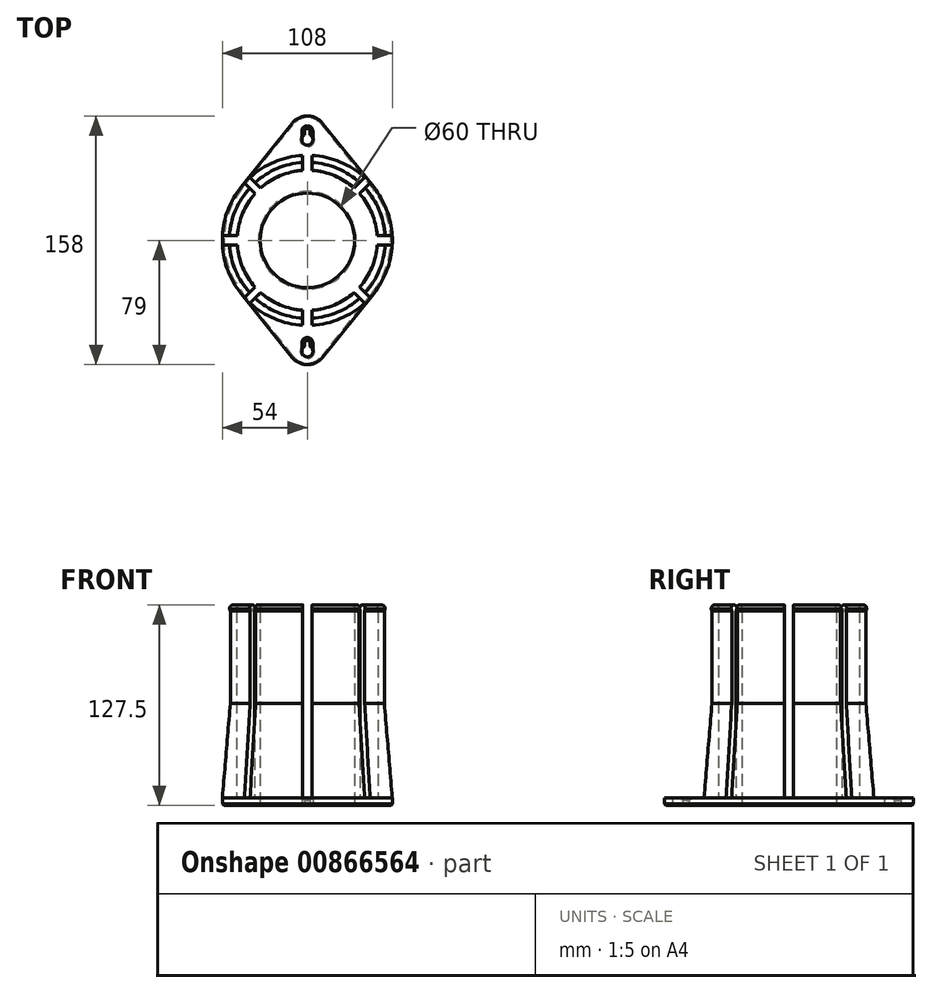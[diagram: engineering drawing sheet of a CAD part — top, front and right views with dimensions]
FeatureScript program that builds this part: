
annotation { "Feature Type Name" : "Feature", "Feature Type Description" : "" }
export const myFeature = defineFeature(function(context is Context, id is Id, definition is map)
    precondition{}
    {
        {
            assignVariable(context, id + "F0", {"name" : "plate", "anyValue" : 5});
        }
        {
            var Q0;
            Q0=qCreatedBy(makeId("Front.planeOp"),FACE);
            var sketch = newSketch(context, id + "F1", { "sketchPlane" : qUnion([Q0])});
            skLineSegment(sketch, "E0.bottom", {"start": v(0, 0) * mm, "end": v(-54, 0) * mm});
            skLineSegment(sketch, "E0.top", {"start": v(0, 5) * mm, "end": v(-54, 5) * mm});
            skLineSegment(sketch, "E0.left", {"start": v(0, 0) * mm, "end": v(0, 5) * mm});
            skLineSegment(sketch, "E0.right", {"start": v(-54, 0) * mm, "end": v(-54, 5) * mm});
            skLineSegment(sketch, "E1", {"start": v(-45, 125) * mm, "end": v(-49, 125) * mm});
            skArc(sketch, "E2", {"start": v(-49, 123.5) * mm, "mid": v(-47, 122.5) * mm, "end": v(-45, 123.5) * mm});
            skLineSegment(sketch, "E3", {"start": v(-47, 125) * mm, "end": v(-41.45, 125) * mm, "construction": true});
            skLineSegment(sketch, "E4", {"start": v(-47, 125) * mm, "end": v(-55.3, 125) * mm, "construction": true});
            skLineSegment(sketch, "E5", {"start": v(-49.5, 125) * mm, "end": v(-49, 123.5) * mm});
            skLineSegment(sketch, "E6", {"start": v(-45, 123.5) * mm, "end": v(-44.5, 125) * mm});
            skArc(sketch, "E7.trimOffspring", {"start": v(-44.5, 125) * mm, "mid": v(-47, 127.5) * mm, "end": v(-49.5, 125) * mm});
            skLineSegment(sketch, "E8", {"start": v(-45, 123.5) * mm, "end": v(-45, 5) * mm});
            skLineSegment(sketch, "E9", {"start": v(-49, 123.5) * mm, "end": v(-49, 5) * mm});
            skLineSegment(sketch, "E10", {"start": v(-54, 5) * mm, "end": v(-49, 65) * mm});
            skLineSegment(sketch, "E11", {"start": v(0, 0) * mm, "end": v(0, 112.8) * mm, "construction": true});
            skSolve(sketch);
        }
        {
            var Q0;
            Q0 = qSketchRegion(id + "F1", true);
            var Q1;
            Q1=sQuery(id+"F1.wireOp",EDGE,"E11");
            revolve(context, id + "F2", {"surfaceOperationType" : NewSurfaceOperationType.NEW, "entities" : qUnion([Q0]), "axis" : qUnion([Q1]), "revolveType" : RevolveType.FULL});
        }
        {
            var Q0;
            Q0=qCreatedBy(makeId("Top.planeOp"),FACE);
            var sketch = newSketch(context, id + "F3", { "sketchPlane" : qUnion([Q0])});
            skArc(sketch, "E12", {"start": v(9.77, 74.3) * mm, "mid": v(0, 79) * mm, "end": v(-9.77, 74.3) * mm});
            skArc(sketch, "E13", {"start": v(-42.2, 33.7) * mm, "mid": v(-54, 0) * mm, "end": v(-42.2, -33.7) * mm});
            skLineSegment(sketch, "E14", {"start": v(-72.22, 0) * mm, "end": v(71.62, 0) * mm, "construction": true});
            skLineSegment(sketch, "E15", {"start": v(-9.77, 74.3) * mm, "end": v(-42.2, 33.7) * mm});
            skLineSegment(sketch, "E16", {"start": v(9.77, 74.3) * mm, "end": v(42.2, 33.7) * mm});
            skLineSegment(sketch, "E17.MirrorCS", {"start": v(-9.77, -74.3) * mm, "end": v(-42.2, -33.7) * mm});
            skArc(sketch, "E18.MirrorCS", {"start": v(9.77, -74.3) * mm, "mid": v(0, -79) * mm, "end": v(-9.77, -74.3) * mm});
            skLineSegment(sketch, "E19.MirrorCS", {"start": v(9.77, -74.3) * mm, "end": v(42.2, -33.7) * mm});
            skArc(sketch, "E20.trimOffspring", {"start": v(42.2, -33.7) * mm, "mid": v(54, 0) * mm, "end": v(42.2, 33.7) * mm});
            skCircle(sketch, "E21", {"center": v(0, 0) * mm, "radius": 30 * mm});
            skCircle(sketch, "E22", {"center": v(0, 69.25) * mm, "radius": 1.75 * mm});
            skCircle(sketch, "E23", {"center": v(0, 64) * mm, "radius": 3.5 * mm});
            skCircle(sketch, "E24", {"center": v(0, -70.5) * mm, "radius": 3.5 * mm});
            skCircle(sketch, "E25", {"center": v(0, -65.25) * mm, "radius": 1.75 * mm});
            skLineSegment(sketch, "E26", {"start": v(-1.75, -65.25) * mm, "end": v(-1.75, -67.47) * mm});
            skLineSegment(sketch, "E27", {"start": v(1.75, -65.25) * mm, "end": v(1.75, -67.47) * mm});
            skLineSegment(sketch, "E28", {"start": v(-1.75, 69.25) * mm, "end": v(-1.75, 67.03) * mm});
            skLineSegment(sketch, "E29", {"start": v(1.75, 69.25) * mm, "end": v(1.75, 67.03) * mm});
            skSolve(sketch);
        }
        {
            var Q0;
            Q0 = qSketchRegion(id + "F3", true);
            var Q1;
            {var subQ0=sQuery(id+"F3.wireOp",EDGE,"f2jhoplT-4Byn-C6TP-uQtg-5tTXQIExNbQD");var subQ1=sQuery(id+"F3.wireOp",EDGE,"0pogwlZP-BW9K-9Tnw-1bp1-9pxBOHaQZQxX");var subQ2=makeQuery(id+"F3.imprint","INTERSECT",VERTEX,{"disambiguationData":[OD(0.0)],"derivedFrom":[subQ1,subQ0]});Q1=makeQuery(id+"F3.imprint","IMPRINT",FACE,{"disambiguationData":[TD([[makeQuery(id+"F3.imprint","IMPRINT",EDGE,{"disambiguationData":[TD([[subQ2,-1.0]])],"derivedFrom":subQ1}),-1.0]])]});}
            var Q2;
            {var subQ0=sQuery(id+"F3.wireOp",EDGE,"f2jhoplT-4Byn-C6TP-uQtg-5tTXQIExNbQD");var subQ1=sQuery(id+"F3.wireOp",EDGE,"0pogwlZP-BW9K-9Tnw-1bp1-9pxBOHaQZQxX");var subQ2=makeQuery(id+"F3.imprint","INTERSECT",VERTEX,{"disambiguationData":[OD(0.0)],"derivedFrom":[subQ1,subQ0]});Q2=makeQuery(id+"F3.imprint","IMPRINT",FACE,{"disambiguationData":[TD([[makeQuery(id+"F3.imprint","IMPRINT",EDGE,{"disambiguationData":[TD([[subQ2,1.0]])],"derivedFrom":subQ1}),1.0]])]});}
            extrude(context, id + "F4", {"entities" : qUnion([Q0, Q1, Q2]), "operationType" : NewBodyOperationType.ADD, "depth" : (getVariable(context, 'plate')) * mm, "offsetDistance" : 25 * mm});
        }
        {
            var Q0;
            {var subQ0=sQuery(id+"F3.wireOp",EDGE,"f2jhoplT-4Byn-C6TP-uQtg-5tTXQIExNbQD");var subQ1=sQuery(id+"F3.wireOp",EDGE,"0pogwlZP-BW9K-9Tnw-1bp1-9pxBOHaQZQxX");var subQ2=makeQuery(id+"F3.imprint","INTERSECT",VERTEX,{"disambiguationData":[OD(0.0)],"derivedFrom":[subQ1,subQ0]});Q0=makeQuery(id+"F3.imprint","IMPRINT",FACE,{"disambiguationData":[TD([[makeQuery(id+"F3.imprint","IMPRINT",EDGE,{"disambiguationData":[TD([[subQ2,1.0]])],"derivedFrom":subQ1}),1.0]])]});}
            var Q1;
            {var subQ0=sQuery(id+"F3.wireOp",EDGE,"f2jhoplT-4Byn-C6TP-uQtg-5tTXQIExNbQD");var subQ1=sQuery(id+"F3.wireOp",EDGE,"0pogwlZP-BW9K-9Tnw-1bp1-9pxBOHaQZQxX");var subQ2=makeQuery(id+"F3.imprint","INTERSECT",VERTEX,{"disambiguationData":[OD(0.0)],"derivedFrom":[subQ1,subQ0]});Q1=makeQuery(id+"F3.imprint","IMPRINT",FACE,{"disambiguationData":[TD([[makeQuery(id+"F3.imprint","IMPRINT",EDGE,{"disambiguationData":[TD([[subQ2,-1.0]])],"derivedFrom":subQ1}),-1.0]])]});}
            var Q2;
            Q2=makeQuery(id+"F3.imprint","IMPRINT",FACE,{"disambiguationData":[TD([[makeQuery(id+"F3.imprint","IMPRINT",EDGE,{"derivedFrom":sQuery(id+"F3.wireOp",EDGE,"E21")}),1.0]])]});
            extrude(context, id + "F5", {"entities" : qUnion([Q0, Q1, Q2]), "operationType" : NewBodyOperationType.REMOVE, "depth" : (getVariable(context, 'plate')) * mm, "offsetDistance" : 25 * mm});
        }
        {
            var Q0;
            Q0=qCreatedBy(makeId("Top.planeOp"),FACE);
            var sketch = newSketch(context, id + "F6", { "sketchPlane" : qUnion([Q0])});
            skLineSegment(sketch, "E30.bottom", {"start": v(3, 75) * mm, "end": v(-3, 75) * mm});
            skLineSegment(sketch, "E30.top", {"start": v(3, -75) * mm, "end": v(-3, -75) * mm});
            skLineSegment(sketch, "E30.left", {"start": v(3, 75) * mm, "end": v(3, -75) * mm});
            skLineSegment(sketch, "E30.right", {"start": v(-3, 75) * mm, "end": v(-3, -75) * mm});
            skPoint(sketch, "E30.middle", {"position": v(0, 0) * mm});
            skLineSegment(sketch, "E31", {"start": v(0, 0) * mm, "end": v(63.35, 63.35) * mm, "construction": true});
            skLineSegment(sketch, "E32", {"start": v(0, 0) * mm, "end": v(-59.23, 59.23) * mm, "construction": true});
            skLineSegment(sketch, "E33.MirrorCS", {"start": v(-75, 3) * mm, "end": v(75, 3) * mm});
            skLineSegment(sketch, "E34.MirrorCS", {"start": v(-75, -3) * mm, "end": v(75, -3) * mm});
            skLineSegment(sketch, "E35.MirrorCS", {"start": v(-75, -3) * mm, "end": v(-75, 3) * mm});
            skLineSegment(sketch, "E36.MirrorCS", {"start": v(75, -3) * mm, "end": v(75, 3) * mm});
            skLineSegment(sketch, "E37", {"start": v(-65.2, 68.73) * mm, "end": v(63.85, -60.32) * mm});
            skLineSegment(sketch, "E38", {"start": v(63.85, -60.32) * mm, "end": v(60.32, -63.85) * mm});
            skLineSegment(sketch, "E39", {"start": v(60.32, -63.85) * mm, "end": v(-68.73, 65.2) * mm});
            skLineSegment(sketch, "E40", {"start": v(-68.73, 65.2) * mm, "end": v(-65.2, 68.73) * mm});
            skLineSegment(sketch, "E41", {"start": v(0, 82.14) * mm, "end": v(0, -84.1) * mm, "construction": true});
            skLineSegment(sketch, "E42.MirrorCS", {"start": v(65.2, 68.73) * mm, "end": v(-63.85, -60.32) * mm});
            skLineSegment(sketch, "E43.MirrorCS", {"start": v(-60.32, -63.85) * mm, "end": v(68.73, 65.2) * mm});
            skLineSegment(sketch, "E44.MirrorCS", {"start": v(68.73, 65.2) * mm, "end": v(65.2, 68.73) * mm});
            skLineSegment(sketch, "E45.MirrorCS", {"start": v(-63.85, -60.32) * mm, "end": v(-60.32, -63.85) * mm});
            skSolve(sketch);
        }
        {
            var Q0;
            Q0 = qSketchRegion(id + "F6", true);
            extrude(context, id + "F7", {"entities" : qUnion([Q0]), "operationType" : NewBodyOperationType.REMOVE, "depth" : 150 * mm, "offsetDistance" : 25 * mm, "hasSecondDirection" : true, "secondDirectionOppositeDirection" : false, "secondDirectionDepth" : (getVariable(context, 'plate')) * mm});
        }
        {
            var Q0;
            Q0=makeQuery(id+"F4.opExtrude","CAP_EDGE",EDGE,{"disambiguationData":[OSD([sQuery(id+"F3.wireOp",EDGE,"E22")])],"isStart":false});
            var Q1;
            Q1=makeQuery(id+"F4.opExtrude","CAP_EDGE",EDGE,{"disambiguationData":[OSD([sQuery(id+"F3.wireOp",EDGE,"E25")])],"isStart":false});
            chamfer(context, id + "F8", {"entities" : qUnion([Q0, Q1]), "width" : 1.75 * mm, "tangentPropagation" : true});
        }
        {
            var Q0;
            Q0=makeQuery(id+"F4.boolean.opBoolean","MERGE",FACE,{"derivedFrom":[makeQuery(id+"F2.opRevolve","SWEPT_FACE",FACE,{"disambiguationData":[OSD([sQuery(id+"F1.wireOp",EDGE,"E0.bottom")])]}),makeQuery(id+"F4.opExtrude","CAP_FACE",FACE,{"disambiguationData":[OSD([sQuery(id+"F3.wireOp",EDGE,"E12"),sQuery(id+"F3.wireOp",EDGE,"E13"),sQuery(id+"F3.wireOp",EDGE,"E15"),sQuery(id+"F3.wireOp",EDGE,"E16"),sQuery(id+"F3.wireOp",EDGE,"E17.MirrorCS"),sQuery(id+"F3.wireOp",EDGE,"E18.MirrorCS"),sQuery(id+"F3.wireOp",EDGE,"E19.MirrorCS"),sQuery(id+"F3.wireOp",EDGE,"E20.trimOffspring"),sQuery(id+"F3.wireOp",EDGE,"E21"),sQuery(id+"F3.wireOp",EDGE,"E22"),sQuery(id+"F3.wireOp",EDGE,"E23"),sQuery(id+"F3.wireOp",EDGE,"E24"),sQuery(id+"F3.wireOp",EDGE,"E25"),sQuery(id+"F3.wireOp",EDGE,"E26"),sQuery(id+"F3.wireOp",EDGE,"E27"),sQuery(id+"F3.wireOp",EDGE,"E28"),sQuery(id+"F3.wireOp",EDGE,"E29")])],"isStart":true})]});
            chamfer(context, id + "F9", {"entities" : qUnion([Q0]), "width" : 1 * mm, "tangentPropagation" : true});
        }
    });
